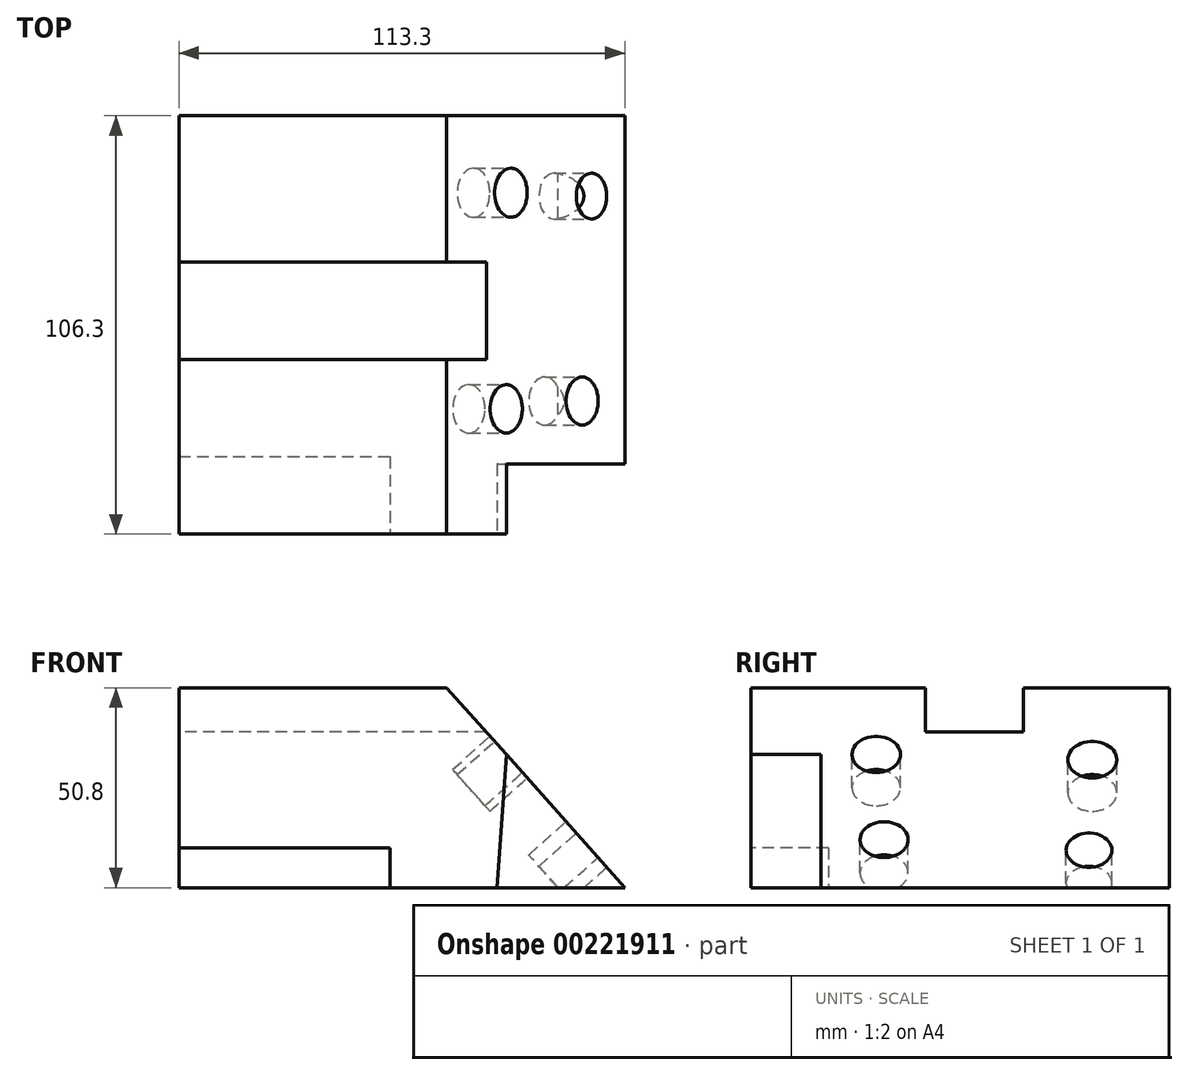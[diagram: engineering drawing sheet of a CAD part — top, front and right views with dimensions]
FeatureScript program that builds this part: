
annotation { "Feature Type Name" : "Feature", "Feature Type Description" : "" }
export const myFeature = defineFeature(function(context is Context, id is Id, definition is map)
    precondition{}
    {
        {
            var Q0;
            Q0=qCreatedBy(makeId("Top.planeOp"),FACE);
            var sketch = newSketch(context, id + "F0", { "sketchPlane" : qUnion([Q0])});
            skLineSegment(sketch, "E0.bottom", {"start": v(45.25, 51.01) * mm, "end": v(-68.05, 51.01) * mm});
            skLineSegment(sketch, "E0.top", {"start": v(45.25, -55.29) * mm, "end": v(-68.05, -55.29) * mm});
            skLineSegment(sketch, "E0.left", {"start": v(45.25, 51.01) * mm, "end": v(45.25, -55.29) * mm});
            skLineSegment(sketch, "E0.right", {"start": v(-68.05, 51.01) * mm, "end": v(-68.05, -55.29) * mm});
            skSolve(sketch);
        }
        {
            var Q0;
            Q0 = qSketchRegion(id + "F0", true);
            extrude(context, id + "F1", {"entities" : qUnion([Q0]), "depth" : 50.8 * mm});
        }
        {
            var Q0;
            Q0=makeQuery(id+"F1.opExtrude","SWEPT_FACE",FACE,{"disambiguationData":[OSD([sQuery(id+"F0.wireOp",EDGE,"E0.top")])]});
            var sketch = newSketch(context, id + "F2", { "sketchPlane" : qUnion([Q0])});
            skLineSegment(sketch, "E1", {"start": v(45.25, 0) * mm, "end": v(0, 50.8) * mm});
            skLineSegment(sketch, "E2", {"start": v(0, 50.8) * mm, "end": v(45.25, 50.8) * mm});
            skLineSegment(sketch, "E3", {"start": v(45.25, 50.8) * mm, "end": v(45.25, 0) * mm});
            skSolve(sketch);
        }
        {
            var Q0;
            Q0 = qSketchRegion(id + "F2", true);
            extrude(context, id + "F3", {"entities" : qUnion([Q0]), "operationType" : NewBodyOperationType.REMOVE, "endBound" : BoundingType.THROUGH_ALL, "oppositeDirection" : true, "depth" : 25.4 * mm});
        }
        {
            var Q0;
            Q0=makeQuery(id+"F1.opExtrude","SWEPT_FACE",FACE,{"disambiguationData":[OSD([sQuery(id+"F0.wireOp",EDGE,"E0.right")])]});
            var sketch = newSketch(context, id + "F4", { "sketchPlane" : qUnion([Q0])});
            skLineSegment(sketch, "E4", {"start": v(-13.91, 50.8) * mm, "end": v(-13.91, 39.5) * mm});
            skLineSegment(sketch, "E5", {"start": v(-13.91, 39.5) * mm, "end": v(10.93, 39.5) * mm});
            skLineSegment(sketch, "E6", {"start": v(10.93, 39.5) * mm, "end": v(10.93, 50.8) * mm});
            skLineSegment(sketch, "E7", {"start": v(10.93, 50.8) * mm, "end": v(-13.91, 50.8) * mm});
            skSolve(sketch);
        }
        {
            var Q0;
            Q0 = qSketchRegion(id + "F4", true);
            extrude(context, id + "F5", {"entities" : qUnion([Q0]), "operationType" : NewBodyOperationType.REMOVE, "endBound" : BoundingType.THROUGH_ALL, "oppositeDirection" : true, "depth" : 25.4 * mm});
        }
        {
            var Q0;
            Q0=makeQuery(id+"F3.boolean.opBoolean","COPY",FACE,{"derivedFrom":makeQuery(id+"F3.opExtrude","SWEPT_FACE",FACE,{"disambiguationData":[OSD([sQuery(id+"F2.wireOp",EDGE,"E1")])]})});
            var sketch = newSketch(context, id + "F6", { "sketchPlane" : qUnion([Q0])});
            skCircle(sketch, "E8", {"center": v(-23.44, 15.24) * mm, "radius": 6.16 * mm});
            skCircle(sketch, "E9", {"center": v(-21.44, -13.76) * mm, "radius": 6.1 * mm});
            skCircle(sketch, "E10", {"center": v(31.46, 13.46) * mm, "radius": 6.23 * mm});
            skCircle(sketch, "E11", {"center": v(30.62, -17.34) * mm, "radius": 5.82 * mm});
            skSolve(sketch);
        }
        {
            var Q0;
            Q0 = qSketchRegion(id + "F6", true);
            extrude(context, id + "F7", {"entities" : qUnion([Q0]), "operationType" : NewBodyOperationType.REMOVE, "oppositeDirection" : true, "depth" : 12.7 * mm});
        }
        {
            var Q0;
            Q0=makeQuery(id+"F1.opExtrude","SWEPT_FACE",FACE,{"disambiguationData":[OSD([sQuery(id+"F0.wireOp",EDGE,"E0.top")])]});
            var sketch = newSketch(context, id + "F8", { "sketchPlane" : qUnion([Q0])});
            skLineSegment(sketch, "E12", {"start": v(12.8, 0) * mm, "end": v(15.11, 33.83) * mm});
            skLineSegment(sketch, "E13", {"start": v(15.11, 33.83) * mm, "end": v(45.25, 0) * mm});
            skLineSegment(sketch, "E14", {"start": v(45.25, 0) * mm, "end": v(12.8, 0) * mm});
            skSolve(sketch);
        }
        {
            var Q0;
            Q0 = qSketchRegion(id + "F8", true);
            extrude(context, id + "F9", {"entities" : qUnion([Q0]), "operationType" : NewBodyOperationType.REMOVE, "oppositeDirection" : true, "depth" : 17.78 * mm});
        }
        {
            var Q0;
            Q0=makeQuery(id+"F1.opExtrude","CAP_FACE",FACE,{"disambiguationData":[OSD([sQuery(id+"F0.wireOp",EDGE,"E0.bottom"),sQuery(id+"F0.wireOp",EDGE,"E0.top"),sQuery(id+"F0.wireOp",EDGE,"E0.left"),sQuery(id+"F0.wireOp",EDGE,"E0.right")])],"isStart":true});
            var sketch = newSketch(context, id + "F10", { "sketchPlane" : qUnion([Q0])});
            skLineSegment(sketch, "E15", {"start": v(-12.2, 55.29) * mm, "end": v(-68.05, 55.29) * mm});
            skLineSegment(sketch, "E16", {"start": v(-68.05, 55.29) * mm, "end": v(-68.05, 29.02) * mm});
            skLineSegment(sketch, "E17", {"start": v(-68.05, 29.02) * mm, "end": v(-68.05, 42.15) * mm});
            skLineSegment(sketch, "E18", {"start": v(-68.05, 42.15) * mm, "end": v(-68.05, 35.59) * mm});
            skLineSegment(sketch, "E19", {"start": v(-68.05, 35.59) * mm, "end": v(-14.44, 35.59) * mm});
            skLineSegment(sketch, "E20", {"start": v(-14.44, 35.59) * mm, "end": v(-14.44, 55.29) * mm});
            skLineSegment(sketch, "E21", {"start": v(-14.44, 55.29) * mm, "end": v(-68.05, 55.29) * mm});
            skSolve(sketch);
        }
        {
            var Q0;
            Q0 = qSketchRegion(id + "F10", true);
            extrude(context, id + "F11", {"entities" : qUnion([Q0]), "operationType" : NewBodyOperationType.REMOVE, "oppositeDirection" : true, "depth" : 10.16 * mm});
        }
    });
